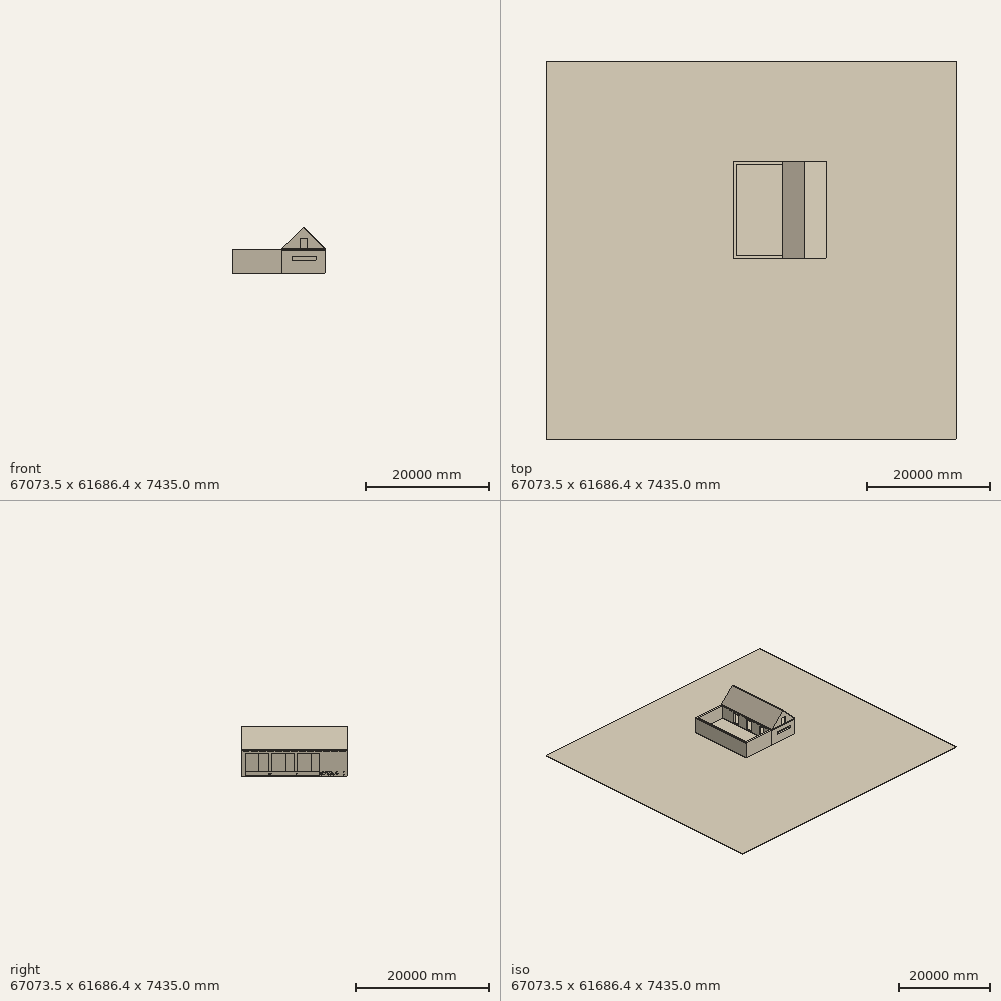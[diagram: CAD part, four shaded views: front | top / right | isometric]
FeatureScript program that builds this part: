
annotation { "Feature Type Name" : "Feature", "Feature Type Description" : "" }
export const myFeature = defineFeature(function(context is Context, id is Id, definition is map)
    precondition{}
    {
        {
            var Q0;
            Q0=qCreatedBy(makeId("Top.planeOp"),FACE);
            var sketch = newSketch(context, id + "F0", { "sketchPlane" : qUnion([Q0])});
            skLineSegment(sketch, "E0.bottom", {"start": v(-3374.35, 6436.17) * mm, "end": v(2825.65, 6436.17) * mm});
            skLineSegment(sketch, "E0.top", {"start": v(-3374.35, -8413.83) * mm, "end": v(2825.65, -8413.83) * mm});
            skLineSegment(sketch, "E0.left", {"start": v(-3374.35, 6436.17) * mm, "end": v(-3374.35, -8413.83) * mm});
            skLineSegment(sketch, "E0.right", {"start": v(2825.65, 6436.17) * mm, "end": v(2825.65, -8413.83) * mm});
            skLineSegment(sketch, "E1.0", {"start": v(-3894.35, 6956.17) * mm, "end": v(-3894.35, -8933.83) * mm});
            skLineSegment(sketch, "E1.1", {"start": v(-3894.35, 6956.17) * mm, "end": v(3345.65, 6956.17) * mm});
            skLineSegment(sketch, "E1.2", {"start": v(3345.65, 6956.17) * mm, "end": v(3345.65, -8933.83) * mm});
            skLineSegment(sketch, "E1.3", {"start": v(-3894.35, -8933.83) * mm, "end": v(3345.65, -8933.83) * mm});
            skLineSegment(sketch, "E2", {"start": v(2825.65, -8413.83) * mm, "end": v(3345.65, -8413.83) * mm});
            skLineSegment(sketch, "E3", {"start": v(2825.65, -4963.83) * mm, "end": v(3345.65, -4963.83) * mm});
            skLineSegment(sketch, "E4", {"start": v(2825.65, -4443.83) * mm, "end": v(3345.65, -4443.83) * mm});
            skLineSegment(sketch, "E5", {"start": v(2825.65, -1063.83) * mm, "end": v(3345.65, -1063.83) * mm});
            skLineSegment(sketch, "E6", {"start": v(2825.65, -543.83) * mm, "end": v(3345.65, -543.83) * mm});
            skLineSegment(sketch, "E7", {"start": v(2825.65, 2696.17) * mm, "end": v(3345.65, 2696.17) * mm});
            skSolve(sketch);
        }
        {
            var Q0;
            {var subQ5=sQuery(id+"F0.wireOp",EDGE,"E0.bottom");Q0=makeQuery(id+"F0.imprint","IMPRINT",FACE,{"disambiguationData":[TD([[makeQuery(id+"F0.imprint","IMPRINT",EDGE,{"derivedFrom":subQ5}),1.0]])]});}
            var Q1;
            {var subQ1=sQuery(id+"F0.wireOp",EDGE,"E0.bottom");Q1=makeQuery(id+"F0.imprint","IMPRINT",FACE,{"disambiguationData":[TD([[makeQuery(id+"F0.imprint","IMPRINT",EDGE,{"derivedFrom":subQ1}),-1.0]])]});}
            var Q2;
            {var subQ0=sQuery(id+"F0.wireOp",EDGE,"E6");Q2=makeQuery(id+"F0.imprint","IMPRINT",FACE,{"disambiguationData":[TD([[makeQuery(id+"F0.imprint","IMPRINT",EDGE,{"derivedFrom":subQ0}),1.0]])]});}
            var Q3;
            {var subQ0=sQuery(id+"F0.wireOp",EDGE,"E5");Q3=makeQuery(id+"F0.imprint","IMPRINT",FACE,{"disambiguationData":[TD([[makeQuery(id+"F0.imprint","IMPRINT",EDGE,{"derivedFrom":subQ0}),1.0]])]});}
            var Q4;
            {var subQ0=sQuery(id+"F0.wireOp",EDGE,"E4");Q4=makeQuery(id+"F0.imprint","IMPRINT",FACE,{"disambiguationData":[TD([[makeQuery(id+"F0.imprint","IMPRINT",EDGE,{"derivedFrom":subQ0}),1.0]])]});}
            var Q5;
            {var subQ0=sQuery(id+"F0.wireOp",EDGE,"E2");Q5=makeQuery(id+"F0.imprint","IMPRINT",FACE,{"disambiguationData":[TD([[makeQuery(id+"F0.imprint","IMPRINT",EDGE,{"derivedFrom":subQ0}),1.0]])]});}
            var Q6;
            {var subQ0=sQuery(id+"F0.wireOp",EDGE,"E3");Q6=makeQuery(id+"F0.imprint","IMPRINT",FACE,{"disambiguationData":[TD([[makeQuery(id+"F0.imprint","IMPRINT",EDGE,{"derivedFrom":subQ0}),1.0]])]});}
            extrude(context, id + "F1", {"entities" : qUnion([Q0, Q1, Q2, Q3, Q4, Q5, Q6]), "oppositeDirection" : true, "depth" : 10 * mm, "offsetDistance" : 25 * mm});
        }
        {
            var Q0;
            {var subQ0=sQuery(id+"F0.wireOp",EDGE,"E5");Q0=makeQuery(id+"F0.imprint","IMPRINT",FACE,{"disambiguationData":[TD([[makeQuery(id+"F0.imprint","IMPRINT",EDGE,{"derivedFrom":subQ0}),1.0]])]});}
            var Q1;
            {var subQ0=sQuery(id+"F0.wireOp",EDGE,"E3");Q1=makeQuery(id+"F0.imprint","IMPRINT",FACE,{"disambiguationData":[TD([[makeQuery(id+"F0.imprint","IMPRINT",EDGE,{"derivedFrom":subQ0}),1.0]])]});}
            var Q2;
            {var subQ5=sQuery(id+"F0.wireOp",EDGE,"E0.bottom");Q2=makeQuery(id+"F0.imprint","IMPRINT",FACE,{"disambiguationData":[TD([[makeQuery(id+"F0.imprint","IMPRINT",EDGE,{"derivedFrom":subQ5}),1.0]])]});}
            extrude(context, id + "F2", {"entities" : qUnion([Q0, Q1, Q2]), "operationType" : NewBodyOperationType.ADD, "depth" : 3350 * mm, "offsetDistance" : 25 * mm});
        }
        {
            var Q0;
            Q0=makeQuery(id+"F2.opExtrude","CAP_FACE",FACE,{"disambiguationData":[OSD([sQuery(id+"F0.wireOp",EDGE,"E0.bottom"),sQuery(id+"F0.wireOp",EDGE,"E0.top"),sQuery(id+"F0.wireOp",EDGE,"E0.left"),sQuery(id+"F0.wireOp",EDGE,"E0.right"),sQuery(id+"F0.wireOp",EDGE,"E1.0"),sQuery(id+"F0.wireOp",EDGE,"E1.1"),sQuery(id+"F0.wireOp",EDGE,"E1.2"),sQuery(id+"F0.wireOp",EDGE,"E1.3"),sQuery(id+"F0.wireOp",EDGE,"E2"),sQuery(id+"F0.wireOp",EDGE,"E7")])],"isStart":false});
            var sketch = newSketch(context, id + "F3", { "sketchPlane" : qUnion([Q0])});
            skLineSegment(sketch, "E8.bottom", {"start": v(-3894.35, 6956.17) * mm, "end": v(3345.65, 6956.17) * mm});
            skLineSegment(sketch, "E8.top", {"start": v(-3894.35, -8933.83) * mm, "end": v(3345.65, -8933.83) * mm});
            skLineSegment(sketch, "E8.left", {"start": v(-3894.35, 6956.17) * mm, "end": v(-3894.35, -8933.83) * mm});
            skLineSegment(sketch, "E8.right", {"start": v(3345.65, 6956.17) * mm, "end": v(3345.65, -8933.83) * mm});
            skLineSegment(sketch, "E9.bottom", {"start": v(2825.65, 6436.17) * mm, "end": v(-3374.35, 6436.17) * mm});
            skLineSegment(sketch, "E9.top", {"start": v(2825.65, -8413.83) * mm, "end": v(-3374.35, -8413.83) * mm});
            skLineSegment(sketch, "E9.left", {"start": v(2825.65, 6436.17) * mm, "end": v(2825.65, -8413.83) * mm});
            skLineSegment(sketch, "E9.right", {"start": v(-3374.35, 6436.17) * mm, "end": v(-3374.35, -8413.83) * mm});
            skSolve(sketch);
        }
        {
            var Q0;
            {var subQ8=sQuery(id+"F3.wireOp",EDGE,"E8.bottom");Q0=makeQuery(id+"F3.imprint","IMPRINT",FACE,{"disambiguationData":[TD([[makeQuery(id+"F3.imprint","IMPRINT",EDGE,{"derivedFrom":subQ8}),-1.0]])]});}
            var Q1;
            {var subQ3=makeQuery(id+"F2.opExtrude","CAP_EDGE",EDGE,{"disambiguationData":[OSD([sQuery(id+"F0.wireOp",EDGE,"E7")])],"isStart":false});Q1=makeQuery(id+"F3.imprint","IMPRINT",FACE,{"disambiguationData":[TD([[makeQuery(id+"F3.imprint","IMPRINT",EDGE,{"derivedFrom":subQ3}),-1.0]])]});}
            extrude(context, id + "F4", {"entities" : qUnion([Q0, Q1]), "operationType" : NewBodyOperationType.ADD, "depth" : 350 * mm, "offsetDistance" : 25 * mm});
        }
        {
            var Q0;
            Q0=makeQuery(id+"F4.opExtrude","CAP_FACE",FACE,{"disambiguationData":[OSD([sQuery(id+"F3.wireOp",EDGE,"E8.bottom"),sQuery(id+"F3.wireOp",EDGE,"E8.top"),sQuery(id+"F3.wireOp",EDGE,"E8.left"),sQuery(id+"F3.wireOp",EDGE,"E8.right"),sQuery(id+"F3.wireOp",EDGE,"E9.bottom"),sQuery(id+"F3.wireOp",EDGE,"E9.top"),sQuery(id+"F3.wireOp",EDGE,"E9.left"),sQuery(id+"F3.wireOp",EDGE,"E9.right")])],"isStart":false});
            var sketch = newSketch(context, id + "F5", { "sketchPlane" : qUnion([Q0])});
            skLineSegment(sketch, "E10.bottom", {"start": v(3345.65, 6956.17) * mm, "end": v(-3894.35, 6956.17) * mm});
            skLineSegment(sketch, "E10.top", {"start": v(3345.65, 6756.17) * mm, "end": v(-3894.35, 6756.17) * mm});
            skLineSegment(sketch, "E10.left", {"start": v(3345.65, 6956.17) * mm, "end": v(3345.65, 6756.17) * mm});
            skLineSegment(sketch, "E10.right", {"start": v(-3894.35, 6956.17) * mm, "end": v(-3894.35, 6756.17) * mm});
            skLineSegment(sketch, "E11.bottom", {"start": v(3345.65, 5749.17) * mm, "end": v(-3894.35, 5749.17) * mm});
            skLineSegment(sketch, "E11.top", {"start": v(3345.65, 5549.17) * mm, "end": v(-3894.35, 5549.17) * mm});
            skLineSegment(sketch, "E11.left", {"start": v(3345.65, 5749.17) * mm, "end": v(3345.65, 5549.17) * mm});
            skLineSegment(sketch, "E11.right", {"start": v(-3894.35, 5749.17) * mm, "end": v(-3894.35, 5549.17) * mm});
            skLineSegment(sketch, "E12.bottom", {"start": v(3345.65, 4542.17) * mm, "end": v(-3894.35, 4542.17) * mm});
            skLineSegment(sketch, "E12.top", {"start": v(3345.65, 4342.17) * mm, "end": v(-3894.35, 4342.17) * mm});
            skLineSegment(sketch, "E12.left", {"start": v(3345.65, 4542.17) * mm, "end": v(3345.65, 4342.17) * mm});
            skLineSegment(sketch, "E12.right", {"start": v(-3894.35, 4542.17) * mm, "end": v(-3894.35, 4342.17) * mm});
            skLineSegment(sketch, "E13.bottom", {"start": v(3345.65, 3335.17) * mm, "end": v(-3894.35, 3335.17) * mm});
            skLineSegment(sketch, "E13.top", {"start": v(3345.65, 3135.17) * mm, "end": v(-3894.35, 3135.17) * mm});
            skLineSegment(sketch, "E13.left", {"start": v(3345.65, 3335.17) * mm, "end": v(3345.65, 3135.17) * mm});
            skLineSegment(sketch, "E13.right", {"start": v(-3894.35, 3335.17) * mm, "end": v(-3894.35, 3135.17) * mm});
            skLineSegment(sketch, "E14.bottom", {"start": v(3345.65, 2128.17) * mm, "end": v(-3894.35, 2128.17) * mm});
            skLineSegment(sketch, "E14.top", {"start": v(3345.65, 1928.17) * mm, "end": v(-3894.35, 1928.17) * mm});
            skLineSegment(sketch, "E14.left", {"start": v(3345.65, 2128.17) * mm, "end": v(3345.65, 1928.17) * mm});
            skLineSegment(sketch, "E14.right", {"start": v(-3894.35, 2128.17) * mm, "end": v(-3894.35, 1928.17) * mm});
            skLineSegment(sketch, "E15.bottom", {"start": v(3345.65, 921.17) * mm, "end": v(-3894.35, 921.17) * mm});
            skLineSegment(sketch, "E15.top", {"start": v(3345.65, 721.17) * mm, "end": v(-3894.35, 721.17) * mm});
            skLineSegment(sketch, "E15.left", {"start": v(3345.65, 921.17) * mm, "end": v(3345.65, 721.17) * mm});
            skLineSegment(sketch, "E15.right", {"start": v(-3894.35, 921.17) * mm, "end": v(-3894.35, 721.17) * mm});
            skLineSegment(sketch, "E16.bottom", {"start": v(3345.65, -285.83) * mm, "end": v(-3894.35, -285.83) * mm});
            skLineSegment(sketch, "E16.top", {"start": v(3345.65, -485.83) * mm, "end": v(-3894.35, -485.83) * mm});
            skLineSegment(sketch, "E16.left", {"start": v(3345.65, -285.83) * mm, "end": v(3345.65, -485.83) * mm});
            skLineSegment(sketch, "E16.right", {"start": v(-3894.35, -285.83) * mm, "end": v(-3894.35, -485.83) * mm});
            skLineSegment(sketch, "E17.bottom", {"start": v(3345.65, -1492.83) * mm, "end": v(-3894.35, -1492.83) * mm});
            skLineSegment(sketch, "E17.top", {"start": v(3345.65, -1692.83) * mm, "end": v(-3894.35, -1692.83) * mm});
            skLineSegment(sketch, "E17.left", {"start": v(3345.65, -1492.83) * mm, "end": v(3345.65, -1692.83) * mm});
            skLineSegment(sketch, "E17.right", {"start": v(-3894.35, -1492.83) * mm, "end": v(-3894.35, -1692.83) * mm});
            skLineSegment(sketch, "E18.bottom", {"start": v(3345.65, -2699.83) * mm, "end": v(-3894.35, -2699.83) * mm});
            skLineSegment(sketch, "E18.top", {"start": v(3345.65, -2899.83) * mm, "end": v(-3894.35, -2899.83) * mm});
            skLineSegment(sketch, "E18.left", {"start": v(3345.65, -2699.83) * mm, "end": v(3345.65, -2899.83) * mm});
            skLineSegment(sketch, "E18.right", {"start": v(-3894.35, -2699.83) * mm, "end": v(-3894.35, -2899.83) * mm});
            skLineSegment(sketch, "E19.bottom", {"start": v(3345.65, -3906.83) * mm, "end": v(-3894.35, -3906.83) * mm});
            skLineSegment(sketch, "E19.top", {"start": v(3345.65, -4106.83) * mm, "end": v(-3894.35, -4106.83) * mm});
            skLineSegment(sketch, "E19.left", {"start": v(3345.65, -3906.83) * mm, "end": v(3345.65, -4106.83) * mm});
            skLineSegment(sketch, "E19.right", {"start": v(-3894.35, -3906.83) * mm, "end": v(-3894.35, -4106.83) * mm});
            skLineSegment(sketch, "E20.bottom", {"start": v(-3894.35, -5113.83) * mm, "end": v(3345.65, -5113.83) * mm});
            skLineSegment(sketch, "E20.top", {"start": v(-3894.35, -5313.83) * mm, "end": v(3345.65, -5313.83) * mm});
            skLineSegment(sketch, "E20.left", {"start": v(-3894.35, -5113.83) * mm, "end": v(-3894.35, -5313.83) * mm});
            skLineSegment(sketch, "E20.right", {"start": v(3345.65, -5113.83) * mm, "end": v(3345.65, -5313.83) * mm});
            skLineSegment(sketch, "E21.bottom", {"start": v(3345.65, -6320.83) * mm, "end": v(-3894.35, -6320.83) * mm});
            skLineSegment(sketch, "E21.top", {"start": v(3345.65, -6520.83) * mm, "end": v(-3894.35, -6520.83) * mm});
            skLineSegment(sketch, "E21.left", {"start": v(3345.65, -6320.83) * mm, "end": v(3345.65, -6520.83) * mm});
            skLineSegment(sketch, "E21.right", {"start": v(-3894.35, -6320.83) * mm, "end": v(-3894.35, -6520.83) * mm});
            skLineSegment(sketch, "E22", {"start": v(-274.35, 5549.17) * mm, "end": v(-274.35, 4542.17) * mm, "construction": true});
            skLineSegment(sketch, "E23", {"start": v(-274.35, 4342.17) * mm, "end": v(-274.35, 3335.17) * mm, "construction": true});
            skLineSegment(sketch, "E24", {"start": v(-274.35, 3135.17) * mm, "end": v(-274.35, 2128.17) * mm, "construction": true});
            skLineSegment(sketch, "E25", {"start": v(-274.35, 1928.17) * mm, "end": v(-274.35, 921.17) * mm, "construction": true});
            skLineSegment(sketch, "E26", {"start": v(-274.35, 721.17) * mm, "end": v(-274.35, -285.83) * mm, "construction": true});
            skLineSegment(sketch, "E27", {"start": v(-274.35, -485.83) * mm, "end": v(-274.35, -1492.83) * mm, "construction": true});
            skLineSegment(sketch, "E28", {"start": v(-274.35, -1692.83) * mm, "end": v(-274.35, -2699.83) * mm, "construction": true});
            skLineSegment(sketch, "E29", {"start": v(-274.35, 5749.17) * mm, "end": v(-274.35, 6756.17) * mm, "construction": true});
            skLineSegment(sketch, "E30", {"start": v(-274.35, -2899.83) * mm, "end": v(-274.35, -3906.83) * mm, "construction": true});
            skLineSegment(sketch, "E31", {"start": v(-274.35, -4106.83) * mm, "end": v(-274.35, -5113.83) * mm, "construction": true});
            skLineSegment(sketch, "E32", {"start": v(-274.35, -5313.83) * mm, "end": v(-274.35, -6320.83) * mm, "construction": true});
            skLineSegment(sketch, "E33.bottom", {"start": v(-3894.35, -7527.83) * mm, "end": v(3345.65, -7527.83) * mm});
            skLineSegment(sketch, "E33.top", {"start": v(-3894.35, -7727.83) * mm, "end": v(3345.65, -7727.83) * mm});
            skLineSegment(sketch, "E33.left", {"start": v(-3894.35, -7527.83) * mm, "end": v(-3894.35, -7727.83) * mm});
            skLineSegment(sketch, "E33.right", {"start": v(3345.65, -7527.83) * mm, "end": v(3345.65, -7727.83) * mm});
            skLineSegment(sketch, "E34.bottom", {"start": v(3345.65, -8734.83) * mm, "end": v(-3894.35, -8734.83) * mm});
            skLineSegment(sketch, "E34.top", {"start": v(3345.65, -8934.83) * mm, "end": v(-3894.35, -8934.83) * mm});
            skLineSegment(sketch, "E34.left", {"start": v(3345.65, -8734.83) * mm, "end": v(3345.65, -8934.83) * mm});
            skLineSegment(sketch, "E34.right", {"start": v(-3894.35, -8734.83) * mm, "end": v(-3894.35, -8934.83) * mm});
            skLineSegment(sketch, "E35", {"start": v(-274.35, -6520.83) * mm, "end": v(-274.35, -7527.83) * mm, "construction": true});
            skLineSegment(sketch, "E36", {"start": v(-274.35, -7727.83) * mm, "end": v(-274.35, -8734.83) * mm, "construction": true});
            skSolve(sketch);
        }
        {
            var Q0;
            Q0=qSketchRegion(id+"F5",true);
            extrude(context, id + "F6", {"entities" : qUnion([Q0]), "operationType" : NewBodyOperationType.ADD, "depth" : 200 * mm, "offsetDistance" : 25 * mm});
        }
        {
            var Q0;
            Q0=makeQuery(id+"F6.opExtrude","CAP_FACE",FACE,{"disambiguationData":[OSD([sQuery(id+"F5.wireOp",EDGE,"E17.bottom"),sQuery(id+"F5.wireOp",EDGE,"E17.top"),sQuery(id+"F5.wireOp",EDGE,"E17.left"),sQuery(id+"F5.wireOp",EDGE,"E17.right")])],"isStart":false});
            var sketch = newSketch(context, id + "F7", { "sketchPlane" : qUnion([Q0])});
            skLineSegment(sketch, "E37.bottom", {"start": v(3345.65, 6956.17) * mm, "end": v(-3894.35, 6956.17) * mm});
            skLineSegment(sketch, "E37.top", {"start": v(3345.65, -8933.83) * mm, "end": v(-3894.35, -8933.83) * mm});
            skLineSegment(sketch, "E37.left", {"start": v(3345.65, 6956.17) * mm, "end": v(3345.65, -8933.83) * mm});
            skLineSegment(sketch, "E37.right", {"start": v(-3894.35, 6956.17) * mm, "end": v(-3894.35, -8933.83) * mm});
            skSolve(sketch);
        }
        {
            var Q0;
            Q0=qSketchRegion(id+"F7",true);
            extrude(context, id + "F8", {"entities" : qUnion([Q0]), "depth" : 3500 * mm, "offsetDistance" : 25 * mm});
        }
        {
            var Q0;
            Q0=makeQuery(id+"F8.opExtrude","CAP_EDGE",EDGE,{"disambiguationData":[OSD([sQuery(id+"F7.wireOp",EDGE,"E37.right")])],"isStart":false});
            var Q1;
            Q1=makeQuery(id+"F8.opExtrude","CAP_EDGE",EDGE,{"disambiguationData":[OSD([sQuery(id+"F7.wireOp",EDGE,"E37.left")])],"isStart":false});
            chamfer(context, id + "F9", {"entities" : qUnion([Q0, Q1]), "chamferType" : ChamferType.TWO_OFFSETS, "width1" : 3600 * mm, "oppositeDirection" : false, "width2" : 3500 * mm, "tangentPropagation" : true});
        }
        {
            var Q0;
            Q0=makeQuery(id+"F8.opExtrude","CAP_FACE",FACE,{"disambiguationData":[OSD([sQuery(id+"F7.wireOp",EDGE,"E37.bottom"),sQuery(id+"F7.wireOp",EDGE,"E37.top"),sQuery(id+"F7.wireOp",EDGE,"E37.left"),sQuery(id+"F7.wireOp",EDGE,"E37.right")])],"isStart":true});
            shell(context, id + "F10", {"entities" : qUnion([Q0]), "thickness" : 260 * mm});
        }
        {
            var Q0;
            Q0=makeQuery(id+"F8.opExtrude","SWEPT_FACE",FACE,{"disambiguationData":[OSD([sQuery(id+"F7.wireOp",EDGE,"E37.top")])]});
            var sketch = newSketch(context, id + "F11", { "sketchPlane" : qUnion([Q0])});
            skLineSegment(sketch, "E38", {"start": v(-274.35, 3900) * mm, "end": v(-274.35, 5889.81) * mm, "construction": true});
            skLineSegment(sketch, "E39.bottom", {"start": v(325.65, 3900) * mm, "end": v(-874.35, 3900) * mm});
            skLineSegment(sketch, "E39.top", {"start": v(325.65, 5600) * mm, "end": v(-874.35, 5600) * mm});
            skLineSegment(sketch, "E39.left", {"start": v(325.65, 3900) * mm, "end": v(325.65, 5600) * mm});
            skLineSegment(sketch, "E39.right", {"start": v(-874.35, 3900) * mm, "end": v(-874.35, 5600) * mm});
            skSolve(sketch);
        }
        {
            var Q0;
            Q0=makeQuery(id+"F11.imprint","IMPRINT",FACE,{"disambiguationData":[TD([[makeQuery(id+"F11.imprint","IMPRINT",EDGE,{"derivedFrom":sQuery(id+"F11.wireOp",EDGE,"E39.bottom")}),-1.0]])]});
            extrude(context, id + "F12", {"entities" : qUnion([Q0]), "operationType" : NewBodyOperationType.REMOVE, "oppositeDirection" : true, "depth" : 260 * mm, "offsetDistance" : 25 * mm});
        }
        {
            var Q0;
            Q0=makeQuery(id+"F1.opExtrude","CAP_FACE",FACE,{"disambiguationData":[OSD([sQuery(id+"F0.wireOp",EDGE,"E1.0"),sQuery(id+"F0.wireOp",EDGE,"E1.1"),sQuery(id+"F0.wireOp",EDGE,"E1.2"),sQuery(id+"F0.wireOp",EDGE,"E1.3")])],"isStart":true});
            var sketch = newSketch(context, id + "F13", { "sketchPlane" : qUnion([Q0])});
            skLineSegment(sketch, "E40.bottom", {"start": v(3345.65, -8413.83) * mm, "end": v(-3374.35, -8413.83) * mm});
            skLineSegment(sketch, "E40.top", {"start": v(3345.65, 6436.17) * mm, "end": v(-3374.35, 6436.17) * mm});
            skLineSegment(sketch, "E40.left", {"start": v(3345.65, -8413.83) * mm, "end": v(3345.65, 6436.17) * mm});
            skLineSegment(sketch, "E40.right", {"start": v(-3374.35, -8413.83) * mm, "end": v(-3374.35, 6436.17) * mm});
            skSolve(sketch);
        }
        {
            var Q0;
            Q0=qSketchRegion(id+"F13",true);
            extrude(context, id + "F14", {"entities" : qUnion([Q0]), "depth" : 700 * mm, "offsetDistance" : 25 * mm});
        }
        {
            var Q0;
            Q0=makeQuery(id+"F6.opExtrude","CAP_FACE",FACE,{"disambiguationData":[OSD([sQuery(id+"F5.wireOp",EDGE,"E10.bottom"),sQuery(id+"F5.wireOp",EDGE,"E10.top"),sQuery(id+"F5.wireOp",EDGE,"E10.left"),sQuery(id+"F5.wireOp",EDGE,"E10.right")])],"isStart":false});
            var sketch = newSketch(context, id + "F15", { "sketchPlane" : qUnion([Q0])});
            skLineSegment(sketch, "E41.bottom", {"start": v(-3894.35, -8934.83) * mm, "end": v(3345.65, -8934.83) * mm});
            skLineSegment(sketch, "E41.top", {"start": v(-3894.35, 6956.17) * mm, "end": v(3345.65, 6956.17) * mm});
            skLineSegment(sketch, "E41.left", {"start": v(-3894.35, -8934.83) * mm, "end": v(-3894.35, 6956.17) * mm});
            skLineSegment(sketch, "E41.right", {"start": v(3345.65, -8934.83) * mm, "end": v(3345.65, 6956.17) * mm});
            skSolve(sketch);
        }
        {
            var Q0;
            Q0=qSketchRegion(id+"F15",true);
            extrude(context, id + "F16", {"entities" : qUnion([Q0]), "depth" : 50 * mm, "offsetDistance" : 25 * mm});
        }
        {
            var Q0;
            {var subQ0=sQuery(id+"F0.wireOp",EDGE,"E1.0");Q0=makeQuery(id+"F6.boolean.opBoolean","MERGE",FACE,{"derivedFrom":[makeQuery(id+"F4.boolean.opBoolean","MERGE",FACE,{"derivedFrom":[makeQuery(id+"F2.boolean.opBoolean","MERGE",FACE,{"derivedFrom":[makeQuery(id+"F1.opExtrude","SWEPT_FACE",FACE,{"disambiguationData":[OSD([subQ0])]}),makeQuery(id+"F2.opExtrude","SWEPT_FACE",FACE,{"disambiguationData":[OSD([subQ0])]})]}),makeQuery(id+"F4.opExtrude","SWEPT_FACE",FACE,{"disambiguationData":[OSD([sQuery(id+"F3.wireOp",EDGE,"E8.left")])]})]}),makeQuery(id+"F6.opExtrude","SWEPT_FACE",FACE,{"disambiguationData":[OSD([sQuery(id+"F5.wireOp",EDGE,"E10.right")])]}),makeQuery(id+"F6.opExtrude","SWEPT_FACE",FACE,{"disambiguationData":[OSD([sQuery(id+"F5.wireOp",EDGE,"E11.right")])]}),makeQuery(id+"F6.opExtrude","SWEPT_FACE",FACE,{"disambiguationData":[OSD([sQuery(id+"F5.wireOp",EDGE,"E12.right")])]}),makeQuery(id+"F6.opExtrude","SWEPT_FACE",FACE,{"disambiguationData":[OSD([sQuery(id+"F5.wireOp",EDGE,"E13.right")])]}),makeQuery(id+"F6.opExtrude","SWEPT_FACE",FACE,{"disambiguationData":[OSD([sQuery(id+"F5.wireOp",EDGE,"E14.right")])]}),makeQuery(id+"F6.opExtrude","SWEPT_FACE",FACE,{"disambiguationData":[OSD([sQuery(id+"F5.wireOp",EDGE,"E15.right")])]}),makeQuery(id+"F6.opExtrude","SWEPT_FACE",FACE,{"disambiguationData":[OSD([sQuery(id+"F5.wireOp",EDGE,"E16.right")])]}),makeQuery(id+"F6.opExtrude","SWEPT_FACE",FACE,{"disambiguationData":[OSD([sQuery(id+"F5.wireOp",EDGE,"E17.right")])]}),makeQuery(id+"F6.opExtrude","SWEPT_FACE",FACE,{"disambiguationData":[OSD([sQuery(id+"F5.wireOp",EDGE,"E18.right")])]}),makeQuery(id+"F6.opExtrude","SWEPT_FACE",FACE,{"disambiguationData":[OSD([sQuery(id+"F5.wireOp",EDGE,"E19.right")])]}),makeQuery(id+"F6.opExtrude","SWEPT_FACE",FACE,{"disambiguationData":[OSD([sQuery(id+"F5.wireOp",EDGE,"E20.left")])]}),makeQuery(id+"F6.opExtrude","SWEPT_FACE",FACE,{"disambiguationData":[OSD([sQuery(id+"F5.wireOp",EDGE,"E21.right")])]}),makeQuery(id+"F6.opExtrude","SWEPT_FACE",FACE,{"disambiguationData":[OSD([sQuery(id+"F5.wireOp",EDGE,"E33.left")])]}),makeQuery(id+"F6.opExtrude","SWEPT_FACE",FACE,{"disambiguationData":[OSD([sQuery(id+"F5.wireOp",EDGE,"E34.right")])]})]});}
            var sketch = newSketch(context, id + "F17", { "sketchPlane" : qUnion([Q0])});
            skLineSegment(sketch, "E42.bottom", {"start": v(6433.83, 3350) * mm, "end": v(4933.83, 3350) * mm});
            skLineSegment(sketch, "E42.top", {"start": v(6433.83, 700) * mm, "end": v(4933.83, 700) * mm});
            skLineSegment(sketch, "E42.left", {"start": v(6433.83, 3350) * mm, "end": v(6433.83, 700) * mm});
            skLineSegment(sketch, "E42.right", {"start": v(4933.83, 3350) * mm, "end": v(4933.83, 700) * mm});
            skPoint(sketch, "E43.oppositeSnap0", {"position": v(5683.83, 700) * mm});
            skLineSegment(sketch, "E44", {"start": v(8413.21, 0) * mm, "end": v(7380.4, 0) * mm, "construction": true});
            skLineSegment(sketch, "E45.bottom", {"start": v(2433.83, 3350) * mm, "end": v(933.83, 3350) * mm});
            skLineSegment(sketch, "E45.top", {"start": v(2433.83, 700) * mm, "end": v(933.83, 700) * mm});
            skLineSegment(sketch, "E45.left", {"start": v(2433.83, 3350) * mm, "end": v(2433.83, 700) * mm});
            skLineSegment(sketch, "E45.right", {"start": v(933.83, 3350) * mm, "end": v(933.83, 700) * mm});
            skLineSegment(sketch, "E46.bottom", {"start": v(-1566.17, 3350) * mm, "end": v(-3066.17, 3350) * mm});
            skLineSegment(sketch, "E46.top", {"start": v(-1566.17, 700) * mm, "end": v(-3066.17, 700) * mm});
            skLineSegment(sketch, "E46.left", {"start": v(-1566.17, 3350) * mm, "end": v(-1566.17, 700) * mm});
            skLineSegment(sketch, "E46.right", {"start": v(-3066.17, 3350) * mm, "end": v(-3066.17, 700) * mm});
            skSolve(sketch);
        }
        {
            var Q0;
            Q0 = qSketchRegion(id + "F17", true);
            extrude(context, id + "F18", {"entities" : qUnion([Q0]), "operationType" : NewBodyOperationType.REMOVE, "oppositeDirection" : true, "depth" : 520 * mm, "offsetDistance" : 25 * mm});
        }
        {
            var Q0;
            {var subQ0=sQuery(id+"F0.wireOp",EDGE,"E1.3");Q0=makeQuery(id+"F4.boolean.opBoolean","MERGE",FACE,{"derivedFrom":[makeQuery(id+"F2.boolean.opBoolean","MERGE",FACE,{"derivedFrom":[makeQuery(id+"F1.opExtrude","SWEPT_FACE",FACE,{"disambiguationData":[OSD([subQ0])]}),makeQuery(id+"F2.opExtrude","SWEPT_FACE",FACE,{"disambiguationData":[OSD([subQ0])]})]}),makeQuery(id+"F4.opExtrude","SWEPT_FACE",FACE,{"disambiguationData":[OSD([sQuery(id+"F3.wireOp",EDGE,"E8.top")])]})]});}
            var sketch = newSketch(context, id + "F19", { "sketchPlane" : qUnion([Q0])});
            skLineSegment(sketch, "E47.bottom", {"start": v(1845.65, 2700) * mm, "end": v(-2154.35, 2700) * mm});
            skLineSegment(sketch, "E47.top", {"start": v(1845.65, 2000) * mm, "end": v(-2154.35, 2000) * mm});
            skLineSegment(sketch, "E47.left", {"start": v(1845.65, 2700) * mm, "end": v(1845.65, 2000) * mm});
            skLineSegment(sketch, "E47.right", {"start": v(-2154.35, 2700) * mm, "end": v(-2154.35, 2000) * mm});
            skLineSegment(sketch, "E48", {"start": v(-471.1, 0) * mm, "end": v(-748.37, 0) * mm, "construction": true});
            skSolve(sketch);
        }
        {
            var Q0;
            Q0 = qSketchRegion(id + "F19", true);
            extrude(context, id + "F20", {"entities" : qUnion([Q0]), "operationType" : NewBodyOperationType.REMOVE, "oppositeDirection" : true, "depth" : 520 * mm, "offsetDistance" : 25 * mm});
        }
        {
            var Q0;
            Q0=makeQuery(id+"F1.opExtrude","CAP_FACE",FACE,{"disambiguationData":[OSD([sQuery(id+"F0.wireOp",EDGE,"E1.0"),sQuery(id+"F0.wireOp",EDGE,"E1.1"),sQuery(id+"F0.wireOp",EDGE,"E1.2"),sQuery(id+"F0.wireOp",EDGE,"E1.3")])],"isStart":false});
            var sketch = newSketch(context, id + "F21", { "sketchPlane" : qUnion([Q0])});
            skLineSegment(sketch, "E49.bottom", {"start": v(24544.78, -23190.92) * mm, "end": v(-42528.7, -23190.92) * mm});
            skLineSegment(sketch, "E49.top", {"start": v(24544.78, 38495.51) * mm, "end": v(-42528.7, 38495.51) * mm});
            skLineSegment(sketch, "E49.left", {"start": v(24544.78, -23190.92) * mm, "end": v(24544.78, 38495.51) * mm});
            skLineSegment(sketch, "E49.right", {"start": v(-42528.7, -23190.92) * mm, "end": v(-42528.7, 38495.51) * mm});
            skSolve(sketch);
        }
        {
            var Q0;
            Q0=makeQuery(id+"F21.imprint","IMPRINT",FACE,{"disambiguationData":[TD([[makeQuery(id+"F21.imprint","IMPRINT",EDGE,{"derivedFrom":sQuery(id+"F21.wireOp",EDGE,"E49.bottom")}),-1.0]])]});
            var Q1;
            Q1=makeQuery(id+"F23.imprint","IMPRINT",FACE,{"disambiguationData":[TD([[makeQuery(id+"F23.imprint","IMPRINT",EDGE,{"derivedFrom":makeQuery(id+"F1.opExtrude","CAP_EDGE",EDGE,{"disambiguationData":[OSD([sQuery(id+"F0.wireOp",EDGE,"E1.0")])],"isStart":false})}),-1.0]])]});
            extrude(context, id + "F22", {"entities" : qUnion([Q0, Q1]), "depth" : 25 * mm, "offsetDistance" : 25 * mm});
        }
        {
            var Q0;
            Q0=makeQuery(id+"F22.opExtrude","CAP_FACE",FACE,{"disambiguationData":[OSD([sQuery(id+"F0.wireOp",EDGE,"E1.0"),sQuery(id+"F0.wireOp",EDGE,"E1.1"),sQuery(id+"F0.wireOp",EDGE,"E1.2"),sQuery(id+"F0.wireOp",EDGE,"E1.3"),sQuery(id+"F21.wireOp",EDGE,"E49.bottom"),sQuery(id+"F21.wireOp",EDGE,"E49.top"),sQuery(id+"F21.wireOp",EDGE,"E49.left"),sQuery(id+"F21.wireOp",EDGE,"E49.right")])],"isStart":true});
            var sketch = newSketch(context, id + "F23", { "sketchPlane" : qUnion([Q0])});
            skLineSegment(sketch, "E50.bottom", {"start": v(-3894.35, 6956.17) * mm, "end": v(-11894.35, 6956.17) * mm});
            skLineSegment(sketch, "E50.top", {"start": v(-3894.35, -8933.83) * mm, "end": v(-11894.35, -8933.83) * mm});
            skLineSegment(sketch, "E50.left", {"start": v(-3894.35, 6956.17) * mm, "end": v(-3894.35, -8933.83) * mm});
            skLineSegment(sketch, "E50.right", {"start": v(-11894.35, 6956.17) * mm, "end": v(-11894.35, -8933.83) * mm});
            skLineSegment(sketch, "E51", {"start": v(-11394.35, -8433.83) * mm, "end": v(-3894.35, -8433.83) * mm});
            skLineSegment(sketch, "E52", {"start": v(-3894.35, 6456.17) * mm, "end": v(-11394.35, 6456.17) * mm});
            skLineSegment(sketch, "E53", {"start": v(-11394.35, 6456.17) * mm, "end": v(-11394.35, -8433.83) * mm});
            skSolve(sketch);
        }
        {
            var Q0;
            {var subQ3=sQuery(id+"F23.wireOp",EDGE,"E50.bottom");Q0=makeQuery(id+"F23.imprint","IMPRINT",FACE,{"disambiguationData":[TD([[makeQuery(id+"F23.imprint","IMPRINT",EDGE,{"derivedFrom":subQ3}),1.0]])]});}
            extrude(context, id + "F24", {"entities" : qUnion([Q0]), "depth" : 3800 * mm, "offsetDistance" : 25 * mm});
        }
        {
            var Q0;
            Q0=makeQuery(id+"F22.opExtrude","CAP_FACE",FACE,{"disambiguationData":[OSD([sQuery(id+"F0.wireOp",EDGE,"E1.0"),sQuery(id+"F0.wireOp",EDGE,"E1.1"),sQuery(id+"F0.wireOp",EDGE,"E1.2"),sQuery(id+"F0.wireOp",EDGE,"E1.3"),sQuery(id+"F21.wireOp",EDGE,"E49.bottom"),sQuery(id+"F21.wireOp",EDGE,"E49.top"),sQuery(id+"F21.wireOp",EDGE,"E49.left"),sQuery(id+"F21.wireOp",EDGE,"E49.right")])],"isStart":true});
            var sketch = newSketch(context, id + "F25", { "sketchPlane" : qUnion([Q0])});
            skLineSegment(sketch, "E54.bottom", {"start": v(-3894.35, 6456.17) * mm, "end": v(-11394.35, 6456.17) * mm});
            skLineSegment(sketch, "E54.top", {"start": v(-3894.35, -8433.83) * mm, "end": v(-11394.35, -8433.83) * mm});
            skLineSegment(sketch, "E54.left", {"start": v(-3894.35, 6456.17) * mm, "end": v(-3894.35, -8433.83) * mm});
            skLineSegment(sketch, "E54.right", {"start": v(-11394.35, 6456.17) * mm, "end": v(-11394.35, -8433.83) * mm});
            skSolve(sketch);
        }
        {
            var Q0;
            Q0=makeQuery(id+"F25.imprint","IMPRINT",FACE,{"disambiguationData":[TD([[makeQuery(id+"F25.imprint","IMPRINT",EDGE,{"derivedFrom":sQuery(id+"F25.wireOp",EDGE,"E54.bottom")}),1.0]])]});
            extrude(context, id + "F26", {"entities" : qUnion([Q0]), "depth" : 700 * mm, "offsetDistance" : 25 * mm});
        }
    });
